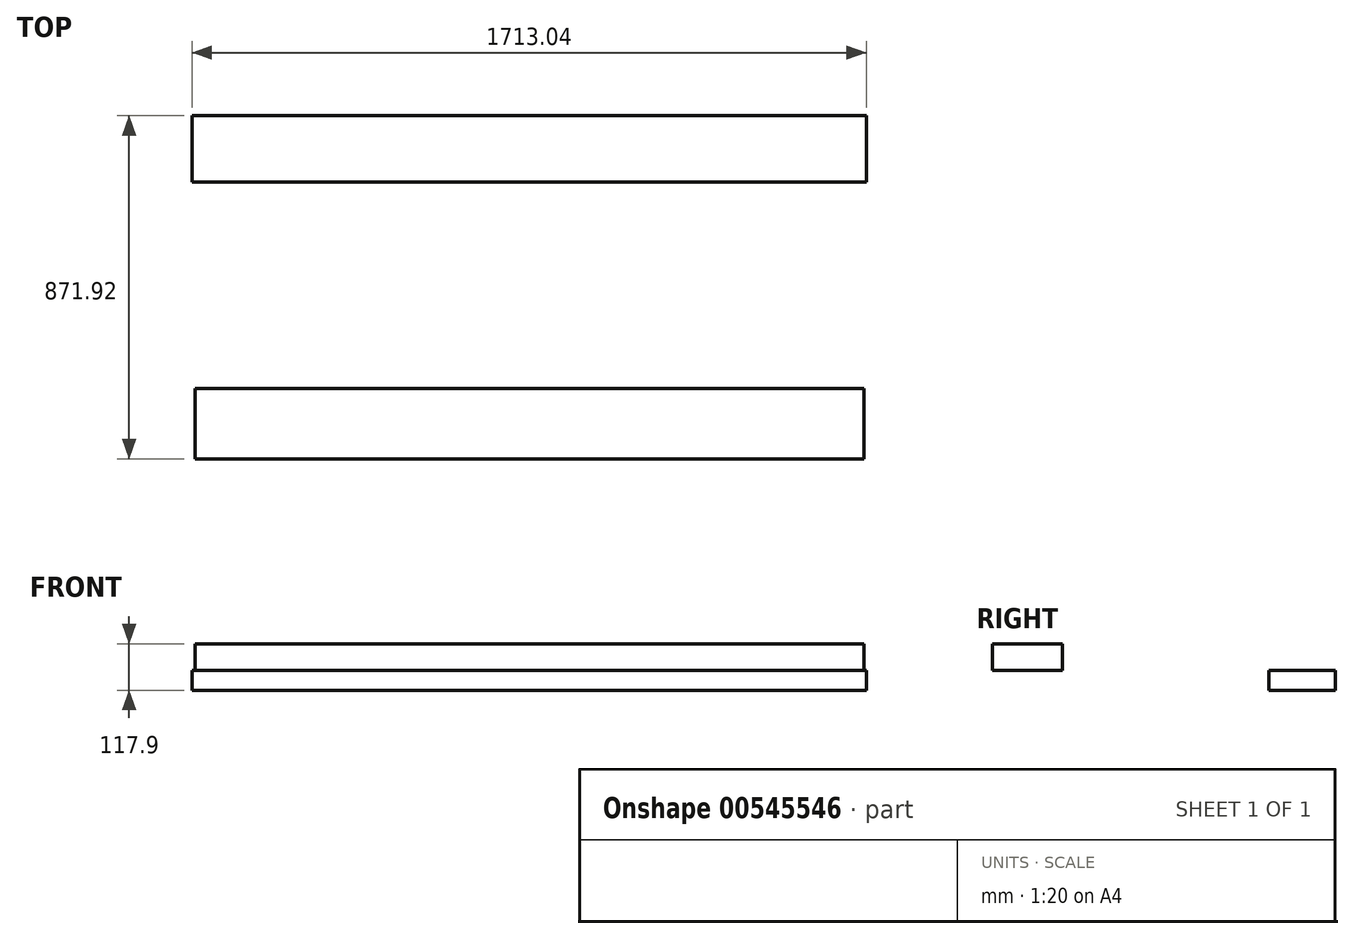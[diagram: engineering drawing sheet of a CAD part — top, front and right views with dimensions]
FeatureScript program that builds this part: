
annotation { "Feature Type Name" : "Feature", "Feature Type Description" : "" }
export const myFeature = defineFeature(function(context is Context, id is Id, definition is map)
    precondition{}
    {
        {
            var Q0;
            Q0=qCreatedBy(makeId("Right.planeOp"),FACE);
            var sketch = newSketch(context, id + "F0", { "sketchPlane" : qUnion([Q0])});
            skLineSegment(sketch, "E0.bottom", {"start": v(89.27, -38.97) * mm, "end": v(-88.95, -38.97) * mm});
            skLineSegment(sketch, "E0.top", {"start": v(89.27, -56.87) * mm, "end": v(-88.95, -56.87) * mm});
            skLineSegment(sketch, "E0.left", {"start": v(89.27, -38.97) * mm, "end": v(89.27, -56.87) * mm});
            skLineSegment(sketch, "E0.right", {"start": v(-88.95, -38.97) * mm, "end": v(-88.95, -56.87) * mm});
            skSolve(sketch);
        }
        {
            var Q0;
            Q0 = qSketchRegion(id + "F0", true);
            extrude(context, id + "F1", {"entities" : qUnion([Q0]), "depth" : 200 * mm, "offsetDistance" : 25.4 * mm});
        }
        {
            var Q0;
            Q0=makeQuery(id+"F1.opExtrude","SWEPT_FACE",FACE,{"disambiguationData":[OSD([sQuery(id+"F0.wireOp",EDGE,"E0.top")])]});
            extrude(context, id + "F2", {"entities" : qUnion([Q0]), "operationType" : NewBodyOperationType.ADD, "depth" : 50 * mm, "offsetDistance" : 25.4 * mm});
        }
        {
            var Q0;
            {var subQ0=sQuery(id+"F0.wireOp",EDGE,"E0.top");Q0=makeQuery(id+"F2.boolean.opBoolean","MERGE",FACE,{"derivedFrom":[makeQuery(id+"F1.opExtrude","CAP_FACE",FACE,{"disambiguationData":[OSD([sQuery(id+"F0.wireOp",EDGE,"E0.bottom"),subQ0,sQuery(id+"F0.wireOp",EDGE,"E0.left"),sQuery(id+"F0.wireOp",EDGE,"E0.right")])],"isStart":true}),makeQuery(id+"F2.opExtrude","SWEPT_FACE",FACE,{"disambiguationData":[OSD([subQ0]),TDD([makeQuery(id+"F1.opExtrude","CAP_EDGE",EDGE,{"disambiguationData":[OSD([subQ0])],"isStart":true})])]})]});}
            extrude(context, id + "F3", {"entities" : qUnion([Q0]), "operationType" : NewBodyOperationType.ADD, "depth" : 1500 * mm, "offsetDistance" : 25.4 * mm});
        }
        {
            var Q0;
            {var subQ0=sQuery(id+"F0.wireOp",EDGE,"E0.top");Q0=makeQuery(id+"F3.boolean.opBoolean","MERGE",FACE,{"derivedFrom":[makeQuery(id+"F2.opExtrude","CAP_FACE",FACE,{"disambiguationData":[OSD([subQ0])],"isStart":false}),makeQuery(id+"F3.opExtrude","SWEPT_FACE",FACE,{"disambiguationData":[OSD([subQ0])]})]});}
            var sketch = newSketch(context, id + "F4", { "sketchPlane" : qUnion([Q0])});
            skLineSegment(sketch, "E1.bottom", {"start": v(-1507.56, -782.97) * mm, "end": v(205.48, -782.97) * mm});
            skLineSegment(sketch, "E1.top", {"start": v(-1507.56, -614.04) * mm, "end": v(205.48, -614.04) * mm});
            skLineSegment(sketch, "E1.left", {"start": v(-1507.56, -782.97) * mm, "end": v(-1507.56, -614.04) * mm});
            skLineSegment(sketch, "E1.right", {"start": v(205.48, -782.97) * mm, "end": v(205.48, -614.04) * mm});
            skSolve(sketch);
        }
        {
            var Q0;
            Q0 = qSketchRegion(id + "F4", true);
            extrude(context, id + "F5", {"entities" : qUnion([Q0]), "depth" : 50 * mm, "offsetDistance" : 25.4 * mm});
        }
    });
